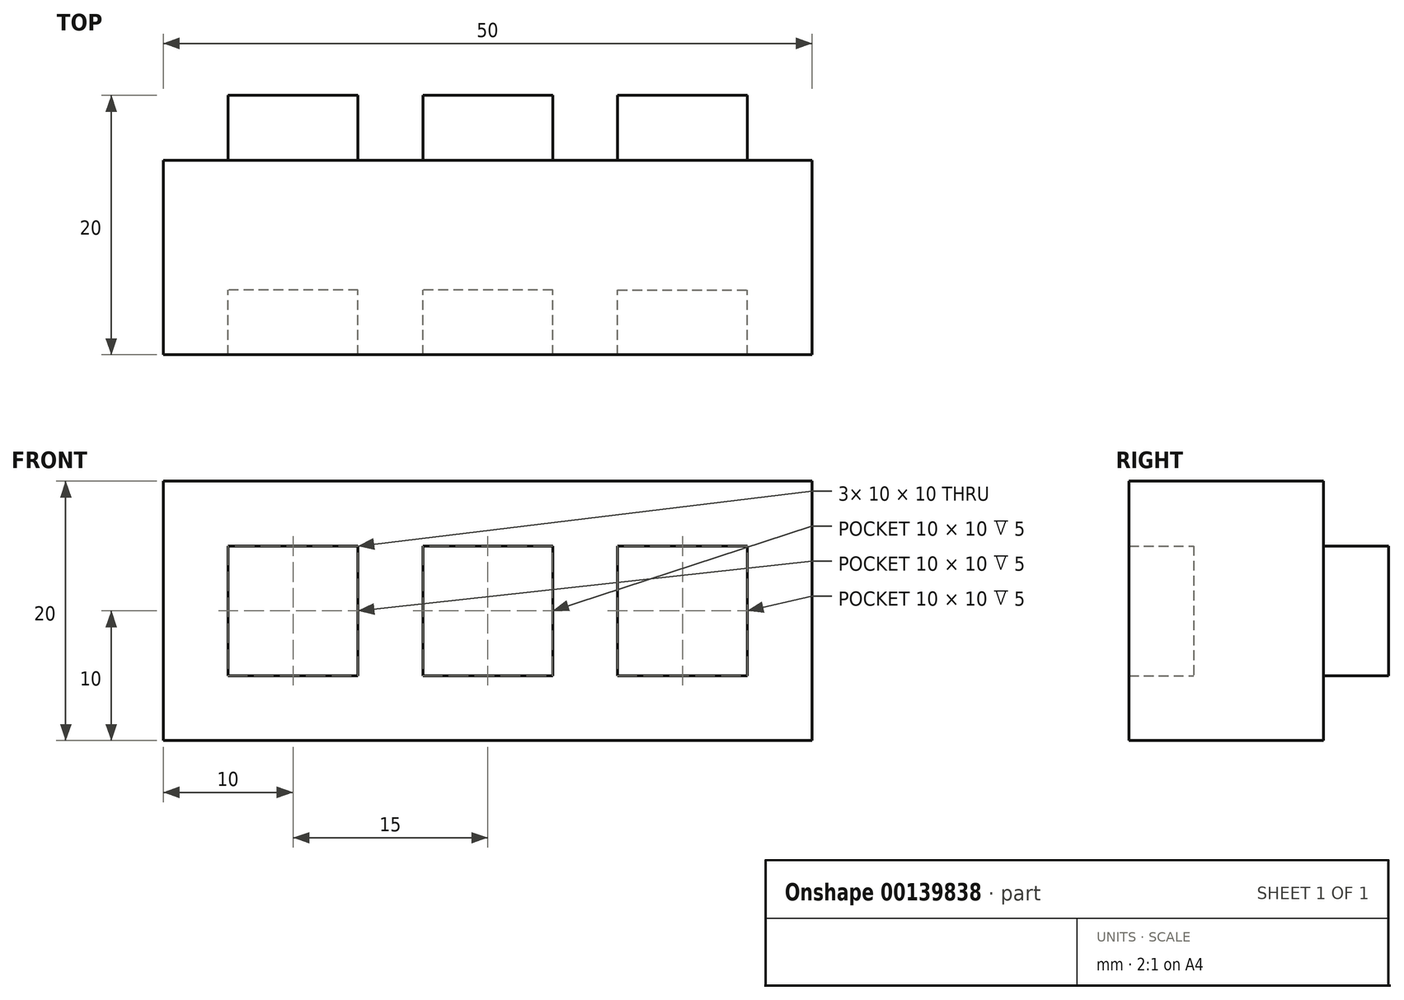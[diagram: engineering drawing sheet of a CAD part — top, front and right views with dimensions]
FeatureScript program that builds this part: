
annotation { "Feature Type Name" : "Feature", "Feature Type Description" : "" }
export const myFeature = defineFeature(function(context is Context, id is Id, definition is map)
    precondition{}
    {
        {
            var Q0;
            Q0=qCreatedBy(makeId("Front.planeOp"),FACE);
            var sketch = newSketch(context, id + "F0", { "sketchPlane" : qUnion([Q0])});
            skLineSegment(sketch, "E0.bottom", {"start": v(25, 10) * mm, "end": v(-25, 10) * mm});
            skLineSegment(sketch, "E0.top", {"start": v(25, -10) * mm, "end": v(-25, -10) * mm});
            skLineSegment(sketch, "E0.left", {"start": v(25, 10) * mm, "end": v(25, -10) * mm});
            skLineSegment(sketch, "E0.right", {"start": v(-25, 10) * mm, "end": v(-25, -10) * mm});
            skPoint(sketch, "E0.middle", {"position": v(0, 0) * mm});
            skLineSegment(sketch, "E1.bottom", {"start": v(5, 5) * mm, "end": v(-5, 5) * mm});
            skLineSegment(sketch, "E1.top", {"start": v(5, -5) * mm, "end": v(-5, -5) * mm});
            skLineSegment(sketch, "E1.left", {"start": v(5, 5) * mm, "end": v(5, -5) * mm});
            skLineSegment(sketch, "E1.right", {"start": v(-5, 5) * mm, "end": v(-5, -5) * mm});
            skLineSegment(sketch, "E2.bottom", {"start": v(-10, 5) * mm, "end": v(-20, 5) * mm});
            skLineSegment(sketch, "E2.top", {"start": v(-10, -5) * mm, "end": v(-20, -5) * mm});
            skLineSegment(sketch, "E2.left", {"start": v(-10, 5) * mm, "end": v(-10, -5) * mm});
            skLineSegment(sketch, "E2.right", {"start": v(-20, 5) * mm, "end": v(-20, -5) * mm});
            skPoint(sketch, "E2.middle", {"position": v(-15, 0) * mm});
            skLineSegment(sketch, "E3.MirrorCS", {"start": v(10, 5) * mm, "end": v(20, 5) * mm});
            skLineSegment(sketch, "E4.MirrorCS", {"start": v(20, 5) * mm, "end": v(20, -5) * mm});
            skLineSegment(sketch, "E5.MirrorCS", {"start": v(10, -5) * mm, "end": v(20, -5) * mm});
            skLineSegment(sketch, "E6.MirrorCS", {"start": v(10, 5) * mm, "end": v(10, -5) * mm});
            skPoint(sketch, "E7.MirrorP", {"position": v(15, 0) * mm});
            skSolve(sketch);
        }
        {
            var Q0;
            Q0 = qSketchRegion(id + "F0", true);
            extrude(context, id + "F1", {"entities" : qUnion([Q0]), "depth" : 5 * mm});
        }
        {
            var Q0;
            Q0=makeQuery(id+"F1.opExtrude","CAP_FACE",FACE,{"disambiguationData":[OSD([sQuery(id+"F0.wireOp",EDGE,"E0.bottom"),sQuery(id+"F0.wireOp",EDGE,"E0.top"),sQuery(id+"F0.wireOp",EDGE,"E0.left"),sQuery(id+"F0.wireOp",EDGE,"E0.right"),sQuery(id+"F0.wireOp",EDGE,"E1.bottom"),sQuery(id+"F0.wireOp",EDGE,"E1.top"),sQuery(id+"F0.wireOp",EDGE,"E1.left"),sQuery(id+"F0.wireOp",EDGE,"E1.right"),sQuery(id+"F0.wireOp",EDGE,"E2.bottom"),sQuery(id+"F0.wireOp",EDGE,"E2.top"),sQuery(id+"F0.wireOp",EDGE,"E2.left"),sQuery(id+"F0.wireOp",EDGE,"E2.right"),sQuery(id+"F0.wireOp",EDGE,"E3.MirrorCS"),sQuery(id+"F0.wireOp",EDGE,"E4.MirrorCS"),sQuery(id+"F0.wireOp",EDGE,"E5.MirrorCS"),sQuery(id+"F0.wireOp",EDGE,"E6.MirrorCS")])],"isStart":true});
            var sketch = newSketch(context, id + "F2", { "sketchPlane" : qUnion([Q0])});
            skLineSegment(sketch, "E8.bottom", {"start": v(-25, 10) * mm, "end": v(25, 10) * mm});
            skLineSegment(sketch, "E8.top", {"start": v(-25, -10) * mm, "end": v(25, -10) * mm});
            skLineSegment(sketch, "E8.left", {"start": v(-25, 10) * mm, "end": v(-25, -10) * mm});
            skLineSegment(sketch, "E8.right", {"start": v(25, 10) * mm, "end": v(25, -10) * mm});
            skSolve(sketch);
        }
        {
            var Q0;
            Q0 = qSketchRegion(id + "F2", true);
            extrude(context, id + "F3", {"entities" : qUnion([Q0]), "operationType" : NewBodyOperationType.ADD, "depth" : 10 * mm});
        }
        {
            var Q0;
            Q0=makeQuery(id+"F3.opExtrude","CAP_FACE",FACE,{"disambiguationData":[OSD([sQuery(id+"F2.wireOp",EDGE,"E8.bottom"),sQuery(id+"F2.wireOp",EDGE,"E8.top"),sQuery(id+"F2.wireOp",EDGE,"E8.left"),sQuery(id+"F2.wireOp",EDGE,"E8.right")])],"isStart":false});
            var sketch = newSketch(context, id + "F4", { "sketchPlane" : qUnion([Q0])});
            skLineSegment(sketch, "E9.bottom", {"start": v(5, 5) * mm, "end": v(-5, 5) * mm});
            skLineSegment(sketch, "E9.top", {"start": v(5, -5) * mm, "end": v(-5, -5) * mm});
            skLineSegment(sketch, "E9.left", {"start": v(5, 5) * mm, "end": v(5, -5) * mm});
            skLineSegment(sketch, "E9.right", {"start": v(-5, 5) * mm, "end": v(-5, -5) * mm});
            skPoint(sketch, "E9.middle", {"position": v(0, 0) * mm});
            skLineSegment(sketch, "E10.bottom", {"start": v(-20, 5) * mm, "end": v(-10, 5) * mm});
            skLineSegment(sketch, "E10.top", {"start": v(-20, -5) * mm, "end": v(-10, -5) * mm});
            skLineSegment(sketch, "E10.left", {"start": v(-20, 5) * mm, "end": v(-20, -5) * mm});
            skLineSegment(sketch, "E10.right", {"start": v(-10, 5) * mm, "end": v(-10, -5) * mm});
            skPoint(sketch, "E10.middle", {"position": v(-15, 0) * mm});
            skLineSegment(sketch, "E11.MirrorCS", {"start": v(20, 5) * mm, "end": v(10, 5) * mm});
            skLineSegment(sketch, "E12.MirrorCS", {"start": v(20, 5) * mm, "end": v(20, -5) * mm});
            skPoint(sketch, "E13.MirrorP", {"position": v(15, 0) * mm});
            skLineSegment(sketch, "E14.MirrorCS", {"start": v(10, 5) * mm, "end": v(10, -5) * mm});
            skLineSegment(sketch, "E15.MirrorCS", {"start": v(20, -5) * mm, "end": v(10, -5) * mm});
            skSolve(sketch);
        }
        {
            var Q0;
            Q0 = qSketchRegion(id + "F4", true);
            extrude(context, id + "F5", {"entities" : qUnion([Q0]), "operationType" : NewBodyOperationType.ADD, "depth" : 5 * mm});
        }
    });
